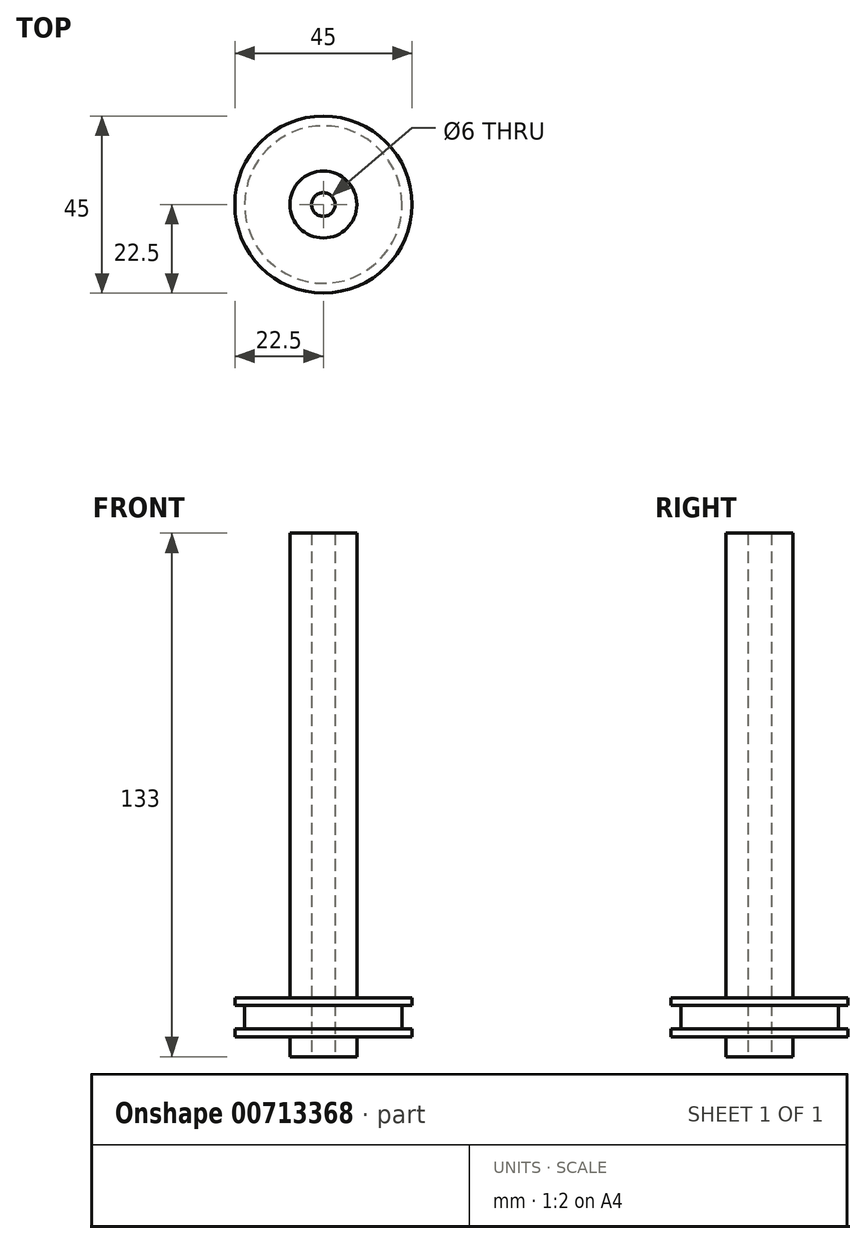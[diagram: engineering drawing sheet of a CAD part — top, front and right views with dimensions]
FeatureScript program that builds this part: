
annotation { "Feature Type Name" : "Feature", "Feature Type Description" : "" }
export const myFeature = defineFeature(function(context is Context, id is Id, definition is map)
    precondition{}
    {
        {
            var Q0;
            Q0=qCreatedBy(makeId("Top.planeOp"),FACE);
            var sketch = newSketch(context, id + "F0", { "sketchPlane" : qUnion([Q0])});
            skCircle(sketch, "E0", {"center": v(0, 0) * mm, "radius": 3 * mm});
            skCircle(sketch, "E1", {"center": v(0, 0) * mm, "radius": 8.5 * mm});
            skCircle(sketch, "E2", {"center": v(0, 0) * mm, "radius": 20 * mm});
            skSolve(sketch);
        }
        {
            var Q0;
            Q0=makeQuery(id+"F0.imprint","IMPRINT",FACE,{"disambiguationData":[TD([[makeQuery(id+"F0.imprint","IMPRINT",EDGE,{"derivedFrom":sQuery(id+"F0.wireOp",EDGE,"E0")}),-1.0]])]});
            extrude(context, id + "F1", {"entities" : qUnion([Q0]), "depth" : 133 * mm, "offsetDistance" : 25 * mm});
        }
        {
            var Q0;
            Q0=makeQuery(id+"F0.imprint","IMPRINT",FACE,{"disambiguationData":[TD([[makeQuery(id+"F0.imprint","IMPRINT",EDGE,{"derivedFrom":sQuery(id+"F0.wireOp",EDGE,"E1")}),-1.0]])]});
            extrude(context, id + "F2", {"entities" : qUnion([Q0]), "operationType" : NewBodyOperationType.ADD, "depth" : 15 * mm, "offsetDistance" : 25 * mm});
        }
        {
            var Q0;
            Q0=makeQuery(id+"F0.imprint","IMPRINT",FACE,{"disambiguationData":[TD([[makeQuery(id+"F0.imprint","IMPRINT",EDGE,{"derivedFrom":sQuery(id+"F0.wireOp",EDGE,"E1")}),-1.0]])]});
            var sketch = newSketch(context, id + "F3", { "sketchPlane" : qUnion([Q0])});
            skCircle(sketch, "E3", {"center": v(0, 0) * mm, "radius": 22.5 * mm});
            skSolve(sketch);
        }
        {
            var Q0;
            Q0 = qSketchRegion(id + "F3", true);
            extrude(context, id + "F4", {"entities" : qUnion([Q0]), "operationType" : NewBodyOperationType.ADD, "depth" : 7 * mm, "offsetDistance" : 25 * mm});
        }
        {
            var Q0;
            Q0=makeQuery(id+"F3.imprint","IMPRINT",FACE,{"disambiguationData":[TD([[makeQuery(id+"F3.imprint","IMPRINT",EDGE,{"derivedFrom":sQuery(id+"F3.wireOp",EDGE,"E3")}),1.0]])]});
            var Q1;
            Q1=makeQuery(id+"F0.imprint","IMPRINT",FACE,{"disambiguationData":[TD([[makeQuery(id+"F0.imprint","IMPRINT",EDGE,{"derivedFrom":sQuery(id+"F0.wireOp",EDGE,"E1")}),-1.0]])]});
            extrude(context, id + "F5", {"entities" : qUnion([Q0, Q1]), "operationType" : NewBodyOperationType.REMOVE, "depth" : 5 * mm, "offsetDistance" : 25 * mm});
        }
        {
            var Q0;
            Q0=makeQuery(id+"F2.opExtrude","CAP_FACE",FACE,{"disambiguationData":[OSD([sQuery(id+"F0.wireOp",EDGE,"E1"),sQuery(id+"F0.wireOp",EDGE,"E2")])],"isStart":false});
            var sketch = newSketch(context, id + "F6", { "sketchPlane" : qUnion([Q0])});
            skCircle(sketch, "E4", {"center": v(0, 0) * mm, "radius": 22.5 * mm});
            skSolve(sketch);
        }
        {
            var Q0;
            Q0=makeQuery(id+"F6.imprint","IMPRINT",FACE,{"disambiguationData":[TD([[makeQuery(id+"F6.imprint","IMPRINT",EDGE,{"derivedFrom":sQuery(id+"F6.wireOp",EDGE,"E4")}),1.0]])]});
            extrude(context, id + "F7", {"entities" : qUnion([Q0]), "operationType" : NewBodyOperationType.ADD, "oppositeDirection" : true, "depth" : 2 * mm, "offsetDistance" : 25 * mm});
        }
        {
            var Q0;
            Q0=makeQuery(id+"F3.imprint","IMPRINT",FACE,{"disambiguationData":[TD([[makeQuery(id+"F3.imprint","IMPRINT",EDGE,{"derivedFrom":makeQuery(id+"F0.imprint","IMPRINT",EDGE,{"derivedFrom":sQuery(id+"F0.wireOp",EDGE,"E1")})}),1.0]])]});
            var sketch = newSketch(context, id + "F8", { "sketchPlane" : qUnion([Q0])});
            skCircle(sketch, "E5", {"center": v(0, 0) * mm, "radius": 3 * mm});
            skSolve(sketch);
        }
        {
            var Q0;
            Q0 = qSketchRegion(id + "F8", true);
            extrude(context, id + "F9", {"entities" : qUnion([Q0]), "operationType" : NewBodyOperationType.REMOVE, "depth" : 140 * mm, "offsetDistance" : 25 * mm});
        }
    });
